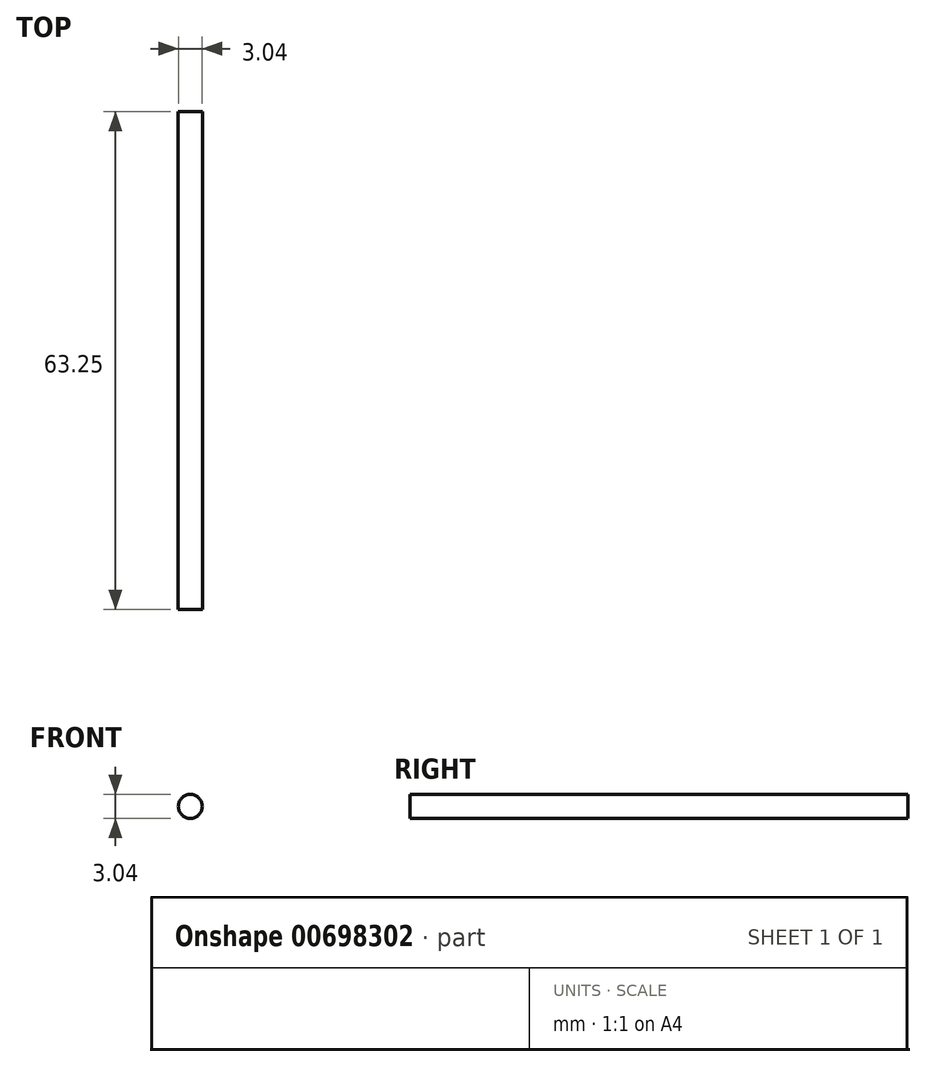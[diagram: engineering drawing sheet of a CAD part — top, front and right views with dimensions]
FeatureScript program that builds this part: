
annotation { "Feature Type Name" : "Feature", "Feature Type Description" : "" }
export const myFeature = defineFeature(function(context is Context, id is Id, definition is map)
    precondition{}
    {
        {
            var Q0;
            Q0=qCreatedBy(makeId("Front.planeOp"),FACE);
            var sketch = newSketch(context, id + "F0", { "sketchPlane" : qUnion([Q0])});
            skCircle(sketch, "E0", {"center": v(0, 0) * mm, "radius": 1.52 * mm});
            skSolve(sketch);
        }
        {
            var Q0;
            Q0=qSketchRegion(id+"F0",true);
            extrude(context, id + "F1", {"entities" : qUnion([Q0]), "depth" : 63.25 * mm, "offsetDistance" : 25.4 * mm});
        }
    });
